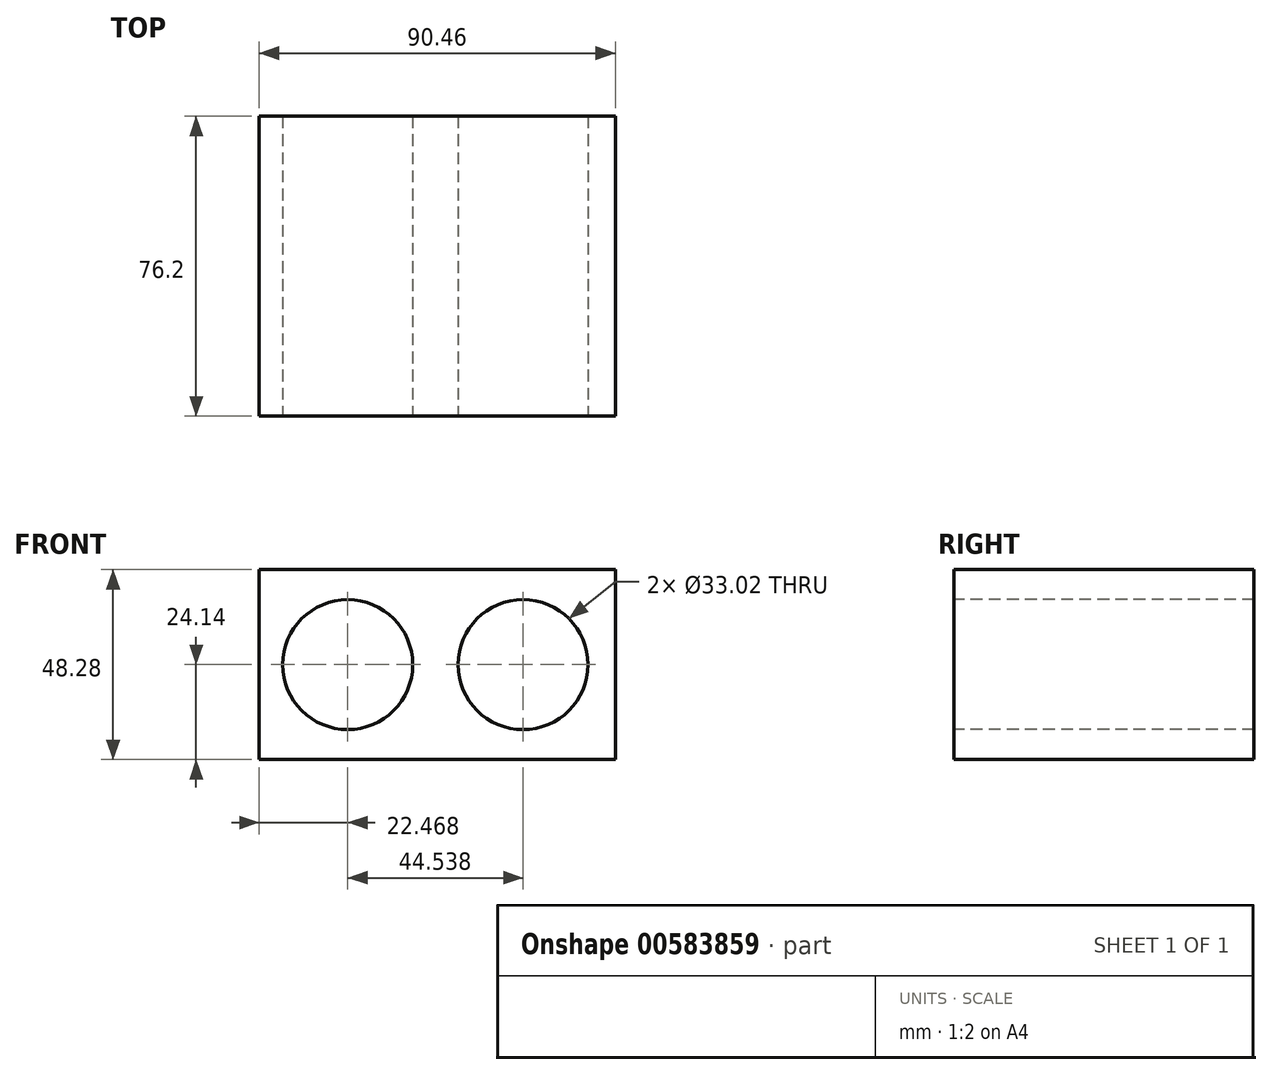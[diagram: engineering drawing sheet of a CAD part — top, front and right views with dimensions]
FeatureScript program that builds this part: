
annotation { "Feature Type Name" : "Feature", "Feature Type Description" : "" }
export const myFeature = defineFeature(function(context is Context, id is Id, definition is map)
    precondition{}
    {
        {
            var Q0;
            Q0=qCreatedBy(makeId("Front.planeOp"),FACE);
            var sketch = newSketch(context, id + "F0", { "sketchPlane" : qUnion([Q0])});
            skLineSegment(sketch, "E0.bottom", {"start": v(45.23, 24.14) * mm, "end": v(-45.23, 24.14) * mm});
            skLineSegment(sketch, "E0.top", {"start": v(45.23, -24.14) * mm, "end": v(-45.23, -24.14) * mm});
            skLineSegment(sketch, "E0.left", {"start": v(45.23, 24.14) * mm, "end": v(45.23, -24.14) * mm});
            skLineSegment(sketch, "E0.right", {"start": v(-45.23, 24.14) * mm, "end": v(-45.23, -24.14) * mm});
            skPoint(sketch, "E0.middle", {"position": v(0, 0) * mm});
            skSolve(sketch);
        }
        {
            var Q0;
            Q0 = qSketchRegion(id + "F0", true);
            extrude(context, id + "F1", {"entities" : qUnion([Q0]), "depth" : 76.2 * mm, "offsetDistance" : 25.4 * mm});
        }
        {
            var Q0;
            Q0=makeQuery(id+"F1.opExtrude","CAP_FACE",FACE,{"disambiguationData":[OSD([sQuery(id+"F0.wireOp",EDGE,"E0.bottom"),sQuery(id+"F0.wireOp",EDGE,"E0.top"),sQuery(id+"F0.wireOp",EDGE,"E0.left"),sQuery(id+"F0.wireOp",EDGE,"E0.right")])],"isStart":false});
            var sketch = newSketch(context, id + "F2", { "sketchPlane" : qUnion([Q0])});
            skPoint(sketch, "E1", {"position": v(-22.76, 0) * mm});
            skPoint(sketch, "E2", {"position": v(21.78, 0) * mm});
            skSolve(sketch);
        }
        {
            var Q0;
            Q0=sQuery(id+"F2.wireOp",VERTEX,"E1");
            var Q1;
            Q1=sQuery(id+"F2.wireOp",VERTEX,"E2");
            var Q2;
            Q2=makeQuery(id+"F1.opExtrude","SWEPT_BODY",BODY,{"disambiguationData":[OSD([sQuery(id+"F0.wireOp",EDGE,"E0.bottom"),sQuery(id+"F0.wireOp",EDGE,"E0.top"),sQuery(id+"F0.wireOp",EDGE,"E0.left"),sQuery(id+"F0.wireOp",EDGE,"E0.right")])]});
            hole(context, id + "F3", {"style" : HoleStyle.SIMPLE, "endStyle" : HoleEndStyle.THROUGH, "holeDiameter" : 33.02 * mm, "majorDiameter" : 6.35 * mm, "isTappedThrough" : true, "tappedDepth" : 12.7 * mm, "tapClearance" : 3, "startFromSketch" : true, "locations" : qUnion([Q0, Q1]), "scope" : qUnion([Q2])});
        }
    });
